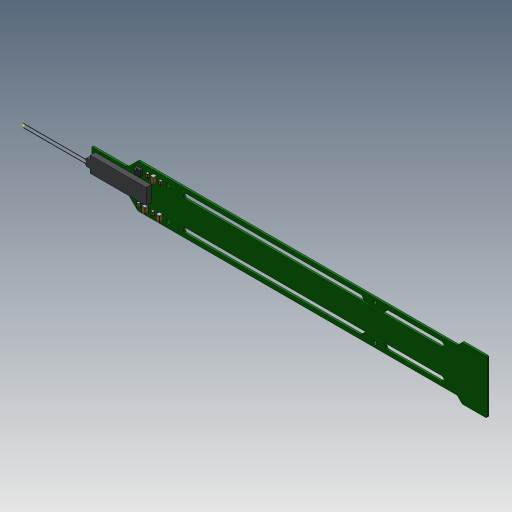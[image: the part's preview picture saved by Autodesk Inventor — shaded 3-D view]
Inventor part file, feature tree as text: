
AUTODESK INVENTOR PART (.ipt)
format: ipt  version: 2023.4 (Build 274418000, 418)  size: 1,504,256 bytes
history: native  units: in
note: dims shown in document units (in); Inventor stores cm internally (conversion verified against a paired STEP export)
features: other x27, extrude x5, plane x2
ambient origin geometry x8: Origin, YZ Plane, XZ Plane, XY Plane, X Axis, Y Axis, Z Axis, Center Point
bodies: Solid1 (feature_tree), Solid2 (feature_tree), Solid3 (feature_tree), Solid4 (feature_tree), Solid5 (feature_tree), Solid6 (feature_tree), Solid7 (feature_tree), Solid8 (feature_tree), Solid9 (feature_tree), Solid10 (feature_tree), Solid11 (feature_tree), Solid12 (feature_tree), Solid13 (feature_tree), Solid14 (feature_tree), Solid15 (feature_tree), Solid16 (feature_tree), Solid17 (feature_tree), Solid18 (feature_tree), Solid19 (feature_tree), Solid20 (feature_tree), Solid21 (feature_tree), Solid22 (feature_tree), Solid23 (feature_tree), Solid24 (feature_tree), Solid25 (feature_tree), Solid26 (feature_tree), Solid27 (feature_tree), Solid28 (feature_tree), Solid29 (feature_tree), Solid30 (feature_tree), Solid31 (feature_tree)
feature tree (34):
  other  "Work Point2- probe center"
  plane  "Work Plane1"
  plane  "Work Plane2"
  other  "Board_1:1"
  other  "CerCap_0402_2:1"
  other  "CerCap_0402_2:2"
  other  "CerCap_0402_2:3"
  extrude  "Extruded_4:1"  [1 undecoded]
  extrude  "Extruded_6:1"  Depth=0.03in
  extrude  "Extruded_6:2"  [1 undecoded]
  other  "Sphere_10:1"
  other  "Sphere_10:2"
  other  "Sphere_10:3"
  other  "Sphere_10:4"
  extrude  "Extruded_15:1"  [1 undecoded]
  extrude  "Extruded_17:1"  [1 undecoded]
  other  "CerCap_0201_20:1"
  other  "CerCap_0201_20:2"
  other  "CerCap_0201_20:3"
  other  "CerCap_0201_22:1"
  other  "CerCap_0201_22:2"
  other  "CerCap_0201_22:3"
  other  "CerCap_0402_24:1"
  other  "CerCap_0402_24:2"
  other  "CerCap_0402_24:3"
  other  "CerCap_0201_26:1"
  other  "CerCap_0201_26:2"
  other  "CerCap_0201_26:3"
  other  "CerCap_0402_28:1"
  other  "CerCap_0402_28:2"
  other  "CerCap_0402_28:3"
  other  "CerCap_0201_30:1"
  other  "CerCap_0201_30:2"
  other  "CerCap_0201_30:3"
note: 4 required parameter values undecoded (feature->parameter linkage not recoverable at this tier; creation-order binding heuristic only, values carry confidence <= 0.55)
